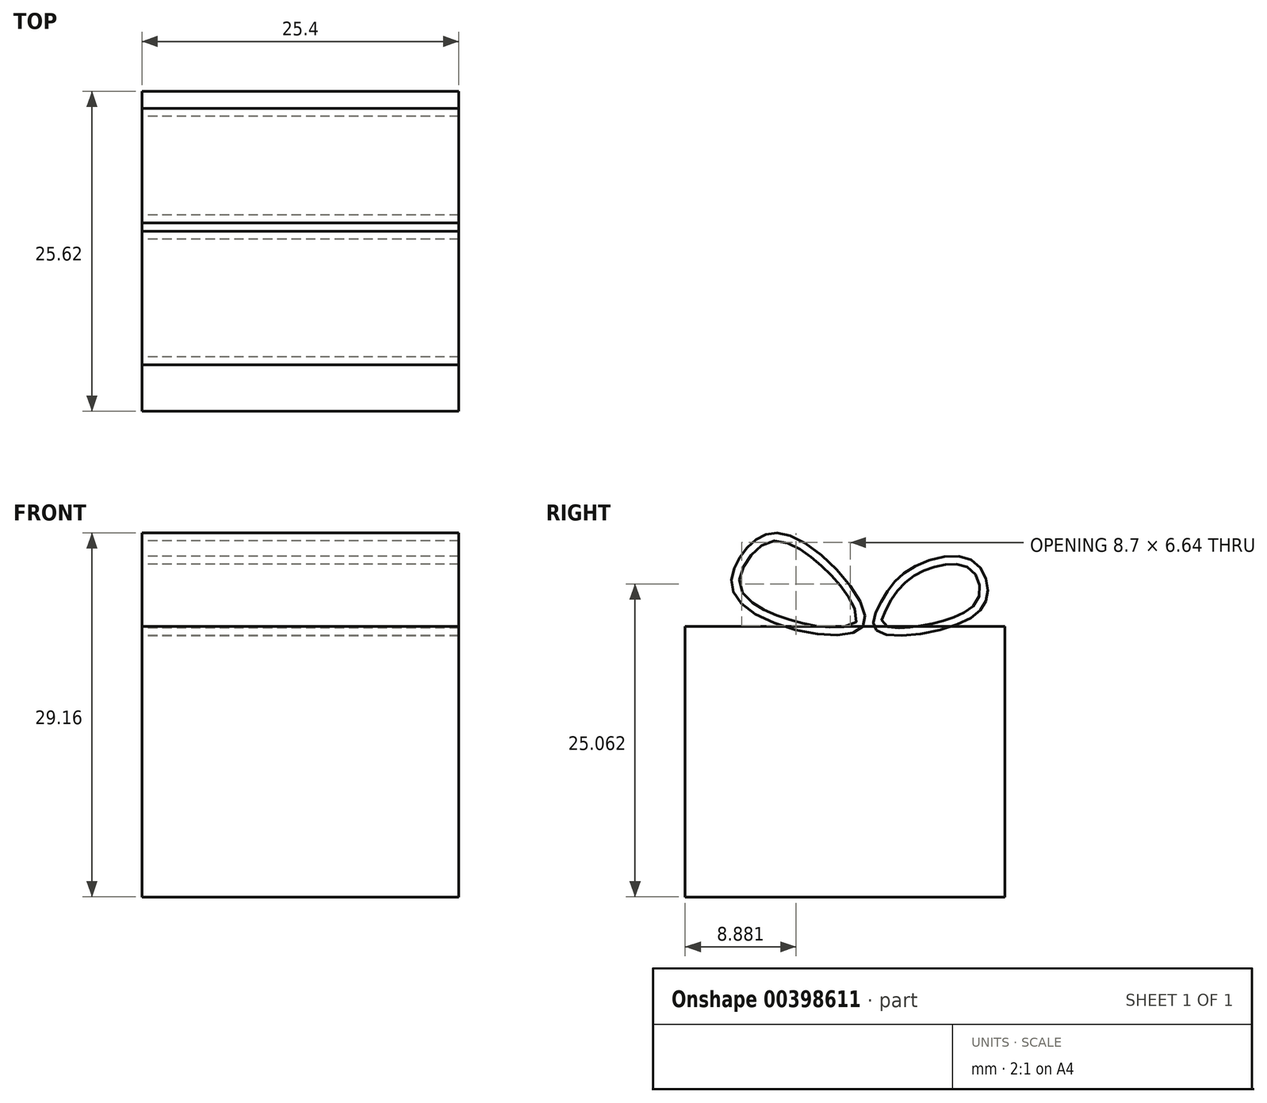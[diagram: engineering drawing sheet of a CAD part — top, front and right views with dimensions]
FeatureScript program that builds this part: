
annotation { "Feature Type Name" : "Feature", "Feature Type Description" : "" }
export const myFeature = defineFeature(function(context is Context, id is Id, definition is map)
    precondition{}
    {
        {
            var Q0;
            Q0=qCreatedBy(makeId("Right.planeOp"),FACE);
            var sketch = newSketch(context, id + "F0", { "sketchPlane" : qUnion([Q0])});
            skLineSegment(sketch, "E0", {"start": v(15.6, 8.9) * mm, "end": v(15.6, -12.76) * mm});
            skLineSegment(sketch, "E1", {"start": v(15.6, -12.76) * mm, "end": v(-10.45, -12.76) * mm});
            skLineSegment(sketch, "E2", {"start": v(-10.02, -13.2) * mm, "end": v(-10.02, 9.34) * mm});
            skLineSegment(sketch, "E3", {"start": v(15.6, 8.9) * mm, "end": v(-10.02, 8.9) * mm});
            skSolve(sketch);
        }
        {
            var Q0;
            Q0=qCreatedBy(makeId("Right.planeOp"),FACE);
            var sketch = newSketch(context, id + "F1", { "sketchPlane" : qUnion([Q0])});
            skFitSpline(sketch, "E4", {"points": [v(4.21, 8.9) * mm, v(-1.35, 16.08) * mm, v(-5.2, 15.04) * mm, v(-5.64, 10.85) * mm, v(4.21, 8.9) * mm]});
            skSolve(sketch);
        }
        {
            var Q0;
            {var subQ0=sQuery(id+"F0.wireOp",EDGE,"E0");Q0=makeQuery(id+"F0.imprint","IMPRINT",FACE,{"disambiguationData":[TD([[makeQuery(id+"F0.imprint","IMPRINT",EDGE,{"derivedFrom":subQ0}),-1.0]])]});}
            extrude(context, id + "F2", {"entities" : qUnion([Q0]), "depth" : 25.4 * mm});
        }
        {
            var Q0;
            Q0 = qSketchRegion(id + "F1", true);
            extrude(context, id + "F3", {"entities" : qUnion([Q0]), "depth" : 25.4 * mm});
        }
        {
            var Q0;
            {var subQ0=sQuery(id+"F0.wireOp",EDGE,"E0");Q0=makeQuery(id+"F0.imprint","IMPRINT",FACE,{"disambiguationData":[TD([[makeQuery(id+"F0.imprint","IMPRINT",EDGE,{"derivedFrom":subQ0}),-1.0]])]});}
            var sketch = newSketch(context, id + "F4", { "sketchPlane" : qUnion([Q0])});
            skFitSpline(sketch, "E5", {"points": [v(5.3, 9.84) * mm, v(5.67, 12.13) * mm, v(8.13, 14.85) * mm, v(12.88, 15.5) * mm, v(14.2, 12.69) * mm, v(11.7, 10.3) * mm, v(5.3, 9.84) * mm]});
            skSolve(sketch);
        }
        {
            var Q0;
            Q0=makeQuery(id+"F4.imprint","IMPRINT",FACE,{"disambiguationData":[TD([[makeQuery(id+"F4.imprint","IMPRINT",EDGE,{"derivedFrom":sQuery(id+"F4.wireOp",EDGE,"E5")}),-1.0]])]});
            extrude(context, id + "F5", {"entities" : qUnion([Q0]), "depth" : 25.4 * mm});
        }
        {
            var Q0;
            Q0=makeQuery(id+"F5.opExtrude","SWEPT_BODY",BODY,{"disambiguationData":[OSD([sQuery(id+"F4.wireOp",EDGE,"E5")])]});
            transform(context, id + "F6", {"entities" : qUnion([Q0]), "transformType" : TransformType.TRANSLATION_3D, "dx" : 0 * mm, "dy" : 0 * mm, "dz" : -1.27 * mm, "makeCopy" : false});
        }
        {
            var Q0;
            Q0=makeQuery(id+"F5.opExtrude","CAP_FACE",FACE,{"disambiguationData":[OSD([sQuery(id+"F4.wireOp",EDGE,"E5")])],"isStart":true});
            var Q1;
            Q1=makeQuery(id+"F5.opExtrude","CAP_FACE",FACE,{"disambiguationData":[OSD([sQuery(id+"F4.wireOp",EDGE,"E5")])],"isStart":false});
            shell(context, id + "F7", {"entities" : qUnion([Q0, Q1]), "thickness" : 0.64 * mm});
        }
        {
            var Q0;
            Q0=makeQuery(id+"F3.opExtrude","CAP_FACE",FACE,{"disambiguationData":[OSD([sQuery(id+"F1.wireOp",EDGE,"E4")])],"isStart":false});
            var Q1;
            Q1=makeQuery(id+"F3.opExtrude","CAP_FACE",FACE,{"disambiguationData":[OSD([sQuery(id+"F1.wireOp",EDGE,"E4")])],"isStart":true});
            shell(context, id + "F8", {"entities" : qUnion([Q0, Q1]), "thickness" : 0.64 * mm});
        }
    });
